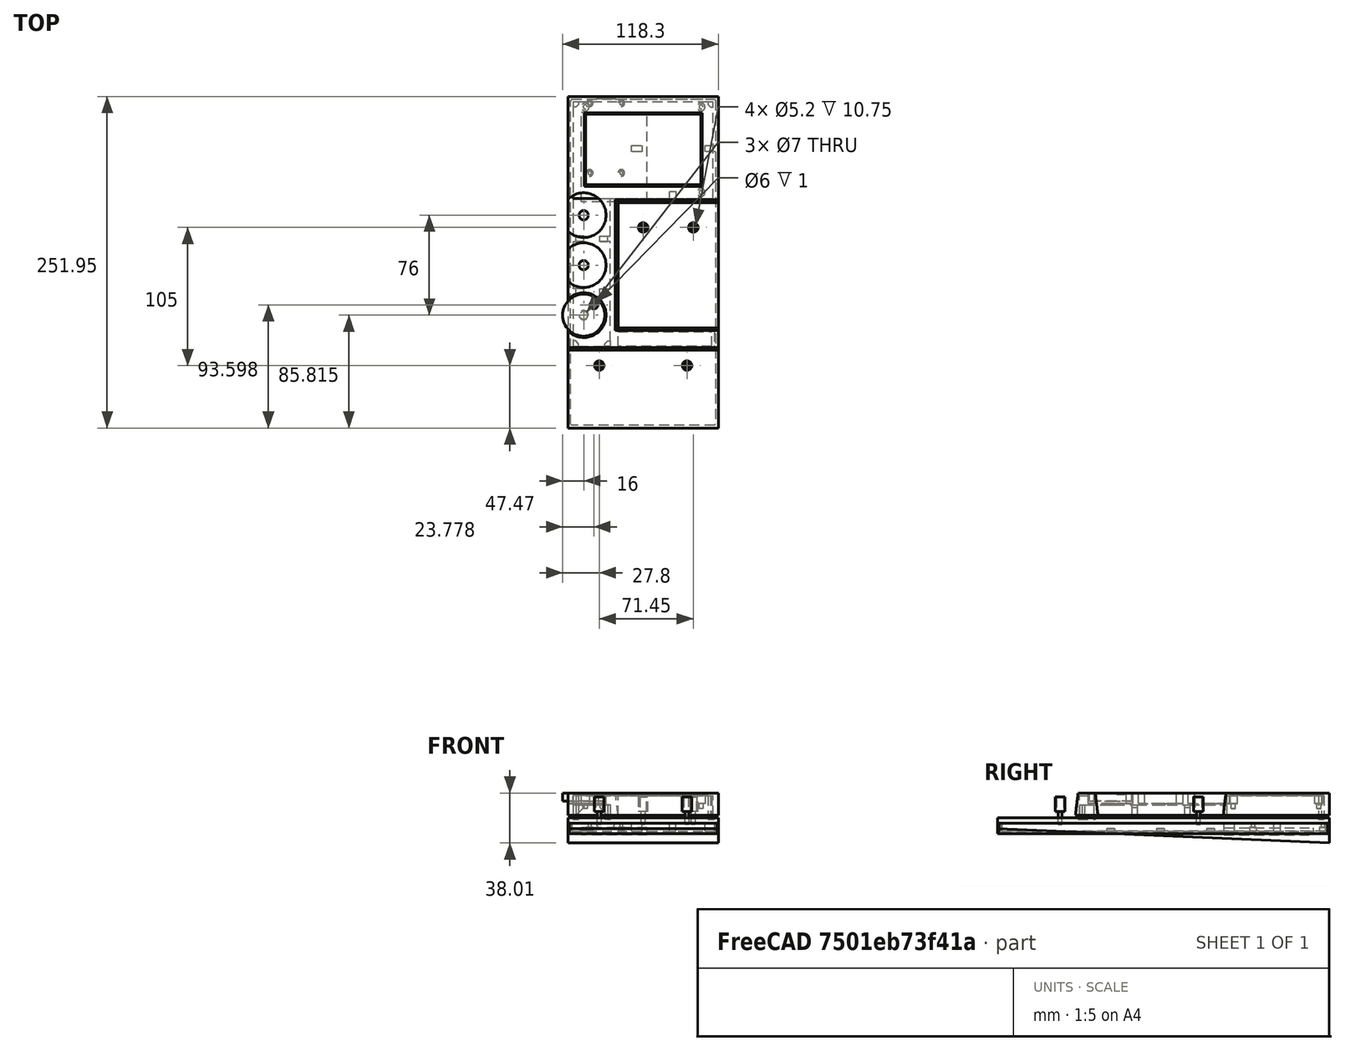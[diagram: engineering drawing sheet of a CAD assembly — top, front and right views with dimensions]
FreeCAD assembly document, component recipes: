
FREECAD ASSEMBLY — COMPONENT RECIPES ("20211026a")

This assembly document has 11 components, labeled P0..P10 below (a component is one placed body or linked part). 10 of them carry a construction recipe — the FreeCAD feature program that regenerates the part from scratch, quoted from this document or its linked companion documents; the rest are supplied as boundary geometry only. No exploded tour is included for this assembly.
COMPONENT P0 — recipe-attached ("TopShell", modeled in this document).
Construction recipe (the document's own serialized feature program — sketch geometry with constraints, then the solid features built on it; lengths are millimeters unless a unit is written):

FEATURE [Sketcher::SketchObject] Sketch005  label="NumpadLoftBottom"
  FullyConstrained = true
  MapMode = 5
  Support = -> [XY_Plane003]
  expr: Constraints[16] = 4 * 19.05
  expr: Constraints[17] = 5 * 19.05
  expr: Constraints[18] = <<var>>.vLCDPad * 2 + 53.7 + 2
  expr: Constraints[15] = <<var>>.vBoxWidth
  sketch-geometry (8):
    g0: LineSegment StartX=0 StartY=0 StartZ=0 EndX=114.3 EndY=0 EndZ=0
    g1: LineSegment StartX=114.3 StartY=0 StartZ=0 EndX=114.3 EndY=-80.5 EndZ=0
    g2: LineSegment StartX=114.3 StartY=-80.5 StartZ=0 EndX=38.1 EndY=-80.5 EndZ=0
    g3: LineSegment StartX=38.1 StartY=-80.5 StartZ=0 EndX=38.1 EndY=-175.75 EndZ=0
    g4: LineSegment StartX=38.1 StartY=-175.75 StartZ=0 EndX=114.3 EndY=-175.75 EndZ=0
    g5: LineSegment StartX=114.3 StartY=-175.75 StartZ=0 EndX=114.3 EndY=-192.8 EndZ=0
    g6: LineSegment StartX=114.3 StartY=-192.8 StartZ=0 EndX=0 EndY=-192.8 EndZ=0
    g7: LineSegment StartX=0 StartY=-192.8 StartZ=0 EndX=0 EndY=0 EndZ=0
  constraints (23):
    c: PointOnObject(g0,g-1)
    c: Coincident(g0,g1)
    c: Vertical(g1)
    c: Coincident(g1,g2)
    c: Horizontal(g2)
    c: Coincident(g2,g3)
    c: Vertical(g3)
    c: Coincident(g3,g4)
    c: Horizontal(g4)
    c: Coincident(g4,g5)
    c: Vertical(g5)
    c: Coincident(g5,g6)
    c: PointOnObject(g6,g-2)
    c: Horizontal(g6)
    c: Coincident(g6,g7)
    c: DistanceX(g6,g6) = 114.3
    c: DistanceX(g4,g4) = 76.2
    c: DistanceY(g3,g3) = 95.25
    c: DistanceY(g1,g1) = 80.5
    c: Equal(g6,g0)
    c: Coincident(g7,g0)
    c: Coincident(g-1,g0)
    c: DistanceY(g5,g5) = 17.05
FEATURE [Sketcher::SketchObject] Sketch006  label="NumpadLoftTop"
  AttachmentOffset = pos=(0,0,17) rot=(0,0,1;0rad)
  FullyConstrained = true
  MapMode = 5
  Placement = pos=(0,0,17) rot=(0,0,1;0rad)
  Support = -> [XY_Plane003]
  expr: Constraints[15] = <<var>>.vBoxWidth
  expr: Constraints[18] = <<var>>.vLCDPad * 2 + 53.7 + 2
  expr: Constraints[17] = 5 * 19.05
  expr: Constraints[16] = 4 * 19.05
  expr: .AttachmentOffset.Base.z = <<var>>.vTopHeight
  sketch-geometry (15):
    g0: LineSegment StartX=0 StartY=0 StartZ=0 EndX=114.3 EndY=0 EndZ=0
    g1: LineSegment StartX=114.3 StartY=0 StartZ=0 EndX=114.3 EndY=-80.5 EndZ=0
    g2: LineSegment StartX=114.3 StartY=-80.5 StartZ=0 EndX=38.1 EndY=-80.5 EndZ=0
    g3: LineSegment StartX=38.1 StartY=-80.5 StartZ=0 EndX=38.1 EndY=-175.75 EndZ=0
    g4: LineSegment StartX=38.1 StartY=-175.75 StartZ=0 EndX=114.3 EndY=-175.75 EndZ=0
    g5: LineSegment StartX=114.3 StartY=-175.75 StartZ=0 EndX=114.3 EndY=-192.8 EndZ=0
    g6: LineSegment StartX=114.3 StartY=-192.8 StartZ=0 EndX=0 EndY=-192.8 EndZ=0
    g7: LineSegment StartX=0 StartY=-192.8 StartZ=0 EndX=0 EndY=0 EndZ=0
    g8: LineSegment StartX=114.3 StartY=0 StartZ=0 EndX=114.3 EndY=-78.5 EndZ=0
    g9: LineSegment StartX=114.3 StartY=-78.5 StartZ=0 EndX=36.1 EndY=-78.5 EndZ=0
    g10: LineSegment StartX=36.1 StartY=-78.5 StartZ=0 EndX=36.1 EndY=-177.75 EndZ=0
    g11: LineSegment StartX=36.1 StartY=-177.75 StartZ=0 EndX=114.3 EndY=-177.75 EndZ=0
    g12: LineSegment StartX=114.3 StartY=-177.75 StartZ=0 EndX=114.3 EndY=-190.8 EndZ=0
    g13: LineSegment StartX=114.3 StartY=-190.8 StartZ=0 EndX=0 EndY=-190.8 EndZ=0
    g14: LineSegment StartX=0 StartY=-190.8 StartZ=0 EndX=0 EndY=0 EndZ=0
  constraints (43):
    c: PointOnObject(g0,g-1)
    c: Coincident(g0,g1)
    c: Vertical(g1)
    c: Coincident(g1,g2)
    c: Horizontal(g2)
    c: Coincident(g2,g3)
    c: Vertical(g3)
    c: Coincident(g3,g4)
    c: Horizontal(g4)
    c: Coincident(g4,g5)
    c: Vertical(g5)
    c: Coincident(g5,g6)
    c: PointOnObject(g6,g-2)
    c: Horizontal(g6)
    c: Coincident(g6,g7)
    c: DistanceX(g6,g6) = 114.3
    c: DistanceX(g4,g4) = 76.2
    c: DistanceY(g3,g3) = 95.25
    c: DistanceY(g1,g1) = 80.5
    c: Equal(g6,g0)
    c: Coincident(g7,g0)
    c: Coincident(g-1,g0)
    c: DistanceY(g5,g5) = 17.05
    c: Coincident(g0,g8)
    c: PointOnObject(g8,g1)
    c: Coincident(g8,g9)
    c: Horizontal(g9)
    c: Coincident(g9,g10)
    c: Vertical(g10)
    c: Coincident(g10,g11)
    c: PointOnObject(g11,g5)
    c: Horizontal(g11)
    c: DistanceY(g2,g9) = 2
    c: DistanceY(g10,g3) = 2
    c: DistanceX(g10,g3) = 2
    c: Coincident(g11,g12)
    c: PointOnObject(g12,g5)
    c: Coincident(g12,g13)
    c: PointOnObject(g13,g7)
    c: Horizontal(g13)
    c: Coincident(g13,g14)
    c: Coincident(g14,g0)
    c: DistanceY(g6,g13) = 2
FEATURE [PartDesign::AdditiveLoft] AdditiveLoft  label="NumpadLoft"
  Closed = false
  Profile = -> Sketch005
  Refine = true
  Ruled = false
  Sections = -> [Sketch006]
FEATURE [Sketcher::SketchObject] Sketch007
  FullyConstrained = true
  MapMode = 5
  Support = -> [XY_Plane003]
  expr: Constraints[8] = <<var>>.vLCDBezWidth
  expr: Constraints[9] = <<var>>.vLCDBezHeight
  expr: Constraints[10] = <<var>>.vLCDPad + 1
  expr: Constraints[11] = <<var>>.vLCDPad + 1
  sketch-geometry (4):
    g0: LineSegment StartX=13.4 StartY=-13.4 StartZ=0 EndX=100.9 EndY=-13.4 EndZ=0
    g1: LineSegment StartX=100.9 StartY=-13.4 StartZ=0 EndX=100.9 EndY=-67.1 EndZ=0
    g2: LineSegment StartX=100.9 StartY=-67.1 StartZ=0 EndX=13.4 EndY=-67.1 EndZ=0
    g3: LineSegment StartX=13.4 StartY=-67.1 StartZ=0 EndX=13.4 EndY=-13.4 EndZ=0
  constraints (12):
    c: Coincident(g0,g1)
    c: Coincident(g1,g2)
    c: Coincident(g2,g3)
    c: Coincident(g3,g0)
    c: Horizontal(g0)
    c: Horizontal(g2)
    c: Vertical(g1)
    c: Vertical(g3)
    c: DistanceX(g0,g0) = 87.5
    c: DistanceY(g3,g3) = 53.7
    c: DistanceX(g-1,g0) = 13.4
    c: DistanceY(g0,g-1) = 13.4
FEATURE [PartDesign::Pocket] Pocket001  label="PocketForScreen"
  BaseFeature = -> AdditiveLoft
  Length = 5
  Length2 = 100
  Profile = -> Sketch007
  Refine = true
  Reversed = true
  Type = 1
FEATURE [PartDesign::Chamfer] Chamfer
  Angle = 45
  Base = -> Pocket001 [Edge30,Edge36,Edge33,Edge35]
  BaseFeature = -> Pocket001
  ChamferType = 0
  FlipDirection = false
  Refine = true
  Size = 1
  Size2 = 1
  SupportTransform = false
FEATURE [PartDesign::Plane] DatumPlane001
  Length = 174.137
  Placement = pos=(0,0,17) rot=(0,0,1;0rad)
  ResizeMode = 0
  Width = 252.637
FEATURE [Sketcher::SketchObject] Sketch008
  ExternalGeometry = -> [Sketch006]
  FullyConstrained = true
  MapMode = 5
  Placement = pos=(0,0,17) rot=(0,0,1;0rad)
  Support = -> [DatumPlane001]
  sketch-geometry (6):
    g0: GeomPoint X=36.1 Y=-128.125 Z=0
    g1: Circle CenterX=12 CenterY=-128.125 CenterZ=0 NormalX=0 NormalY=0 NormalZ=1 AngleXU=0 Radius=17
    g2: Circle CenterX=12 CenterY=-90.125 CenterZ=0 NormalX=0 NormalY=0 NormalZ=1 AngleXU=0 Radius=17
    g3: Circle CenterX=12 CenterY=-166.125 CenterZ=0 NormalX=0 NormalY=0 NormalZ=1 AngleXU=0 Radius=17
    g4: LineSegment StartX=12 StartY=-90.125 StartZ=0 EndX=12 EndY=-128.125 EndZ=0
    g5: LineSegment StartX=12 StartY=-128.125 StartZ=0 EndX=12 EndY=-166.125 EndZ=0
  constraints (14):
    c: Symmetric(g-3,g-3,g0)
    c: Horizontal(g0,g1)
    c: DistanceX(g-1,g1) = 12  'ScrubberOffset'
    c: Equal(g1,g2)
    c: Equal(g1,g3)
    c: Vertical(g1,g3)
    c: Radius(g1) = 17  'ScrubberRadius'
    c: DistanceY(g3,g1) = 38  'ScrubberSpacing'
    c: Vertical(g1,g2)
    c: Coincident(g4,g2)
    c: Coincident(g4,g1)
    c: Coincident(g5,g1)
    c: Coincident(g5,g3)
    c: Equal(g4,g5)
FEATURE [PartDesign::Pocket] Pocket002  label="PocketForScrubbers"
  BaseFeature = -> Chamfer
  Length = 8
  Length2 = 100
  Profile = -> Sketch008
  Refine = true
  Type = 0
FEATURE [PartDesign::Plane] DatumPlane005
  Length = 174.137
  MapMode = 5
  Placement = pos=(0,0,0) rot=(1,0,0;3.14159rad)
  ResizeMode = 0
  Width = 252.637
FEATURE [Sketcher::SketchObject] Sketch022
  ExternalGeometry = -> [Pocket002]
  FullyConstrained = true
  MapMode = 5
  Placement = pos=(0,0,0) rot=(1,0,0;3.14159rad)
  Support = -> [DatumPlane005]
  sketch-geometry (10):
    g0: LineSegment StartX=0 StartY=0 StartZ=0 EndX=114.3 EndY=0 EndZ=0
    g1: LineSegment StartX=114.3 StartY=0 StartZ=0 EndX=114.3 EndY=80.5 EndZ=0
    g2: LineSegment StartX=114.3 StartY=80.5 StartZ=0 EndX=38.1 EndY=80.5 EndZ=0
    g3: LineSegment StartX=38.1 StartY=80.5 StartZ=0 EndX=38.1 EndY=67.1 EndZ=0
    g4: LineSegment StartX=38.1 StartY=67.1 StartZ=0 EndX=0 EndY=67.1 EndZ=0
    g5: LineSegment StartX=0 StartY=67.1 StartZ=0 EndX=0 EndY=0 EndZ=0
    g6: LineSegment StartX=4 StartY=77.5 StartZ=0 EndX=110.3 EndY=77.5 EndZ=0
    g7: LineSegment StartX=110.3 StartY=77.5 StartZ=0 EndX=110.3 EndY=4 EndZ=0
    g8: LineSegment StartX=110.3 StartY=4 StartZ=0 EndX=4 EndY=4 EndZ=0
    g9: LineSegment StartX=4 StartY=4 StartZ=0 EndX=4 EndY=77.5 EndZ=0
  constraints (27):
    c: Coincident(g-1,g0)
    c: PointOnObject(g0,g-1)
    c: Coincident(g0,g1)
    c: Coincident(g1,g-3)
    c: Coincident(g1,g2)
    c: Coincident(g2,g-4)
    c: Coincident(g2,g3)
    c: Vertical(g3)
    c: Coincident(g3,g4)
    c: Horizontal(g4)
    c: Coincident(g4,g5)
    c: Coincident(g5,g0)
    c: Vertical(g5)
    c: Vertical(g1)
    c: Horizontal(g-5,g3)
    c: Horizontal(g6)
    c: Coincident(g6,g7)
    c: Vertical(g7)
    c: Coincident(g7,g8)
    c: Horizontal(g8)
    c: Coincident(g8,g9)
    c: Vertical(g9)
    c: Distance(g6,g1) = 4
    c: Distance(g8,g0) = 4
    c: Distance(g8,g5) = 4
    c: Coincident(g9,g6)
    c: Distance(g6,g2) = 3
FEATURE [PartDesign::Pocket] Pocket006  label="PocketRearLCD"
  BaseFeature = -> Pocket002
  Length = 15
  Length2 = 100
  Profile = -> Sketch022
  Refine = true
  Type = 0
FEATURE [Sketcher::SketchObject] Sketch023
  ExternalGeometry = -> [Pocket006]
  FullyConstrained = true
  MapMode = 5
  Placement = pos=(0,0,0) rot=(1,0,0;3.14159rad)
  Support = -> [DatumPlane005]
  sketch-geometry (4):
    g0: LineSegment StartX=38.1 StartY=178.75 StartZ=0 EndX=111.3 EndY=178.75 EndZ=0
    g1: LineSegment StartX=111.3 StartY=178.75 StartZ=0 EndX=111.3 EndY=189.8 EndZ=0
    g2: LineSegment StartX=111.3 StartY=189.8 StartZ=0 EndX=38.1 EndY=189.8 EndZ=0
    g3: LineSegment StartX=38.1 StartY=189.8 StartZ=0 EndX=38.1 EndY=178.75 EndZ=0
  constraints (12):
    c: Coincident(g0,g1)
    c: Coincident(g1,g2)
    c: Coincident(g2,g3)
    c: Coincident(g3,g0)
    c: Horizontal(g0)
    c: Horizontal(g2)
    c: Vertical(g1)
    c: DistanceX(g1,g-4) = 3
    c: DistanceY(g-3,g0) = 3
    c: DistanceY(g1,g-4) = 3
    c: Vertical(g3)
    c: Vertical(g0,g-3)
FEATURE [PartDesign::Pocket] Pocket007  label="PocketRearChords"
  BaseFeature = -> Pocket006
  Length = 15
  Length2 = 100
  Profile = -> Sketch023
  Refine = true
  Type = 0
FEATURE [Sketcher::SketchObject] Sketch024
  ExternalGeometry = -> [Pocket007]
  FullyConstrained = true
  MapMode = 5
  Placement = pos=(0,0,0) rot=(1,0,0;3.14159rad)
  Support = -> [DatumPlane005]
  sketch-geometry (4):
    g0: LineSegment StartX=4 StartY=189.8 StartZ=0 EndX=32.1 EndY=189.8 EndZ=0
    g1: LineSegment StartX=32.1 StartY=189.8 StartZ=0 EndX=32.1 EndY=75.125 EndZ=0
    g2: LineSegment StartX=32.1 StartY=75.125 StartZ=0 EndX=4 EndY=75.125 EndZ=0
    g3: LineSegment StartX=4 StartY=75.125 StartZ=0 EndX=4 EndY=189.8 EndZ=0
  constraints (11):
    c: Coincident(g0,g1)
    c: Coincident(g1,g2)
    c: Coincident(g2,g3)
    c: Coincident(g3,g0)
    c: Horizontal(g0)
    c: Horizontal(g2)
    c: Vertical(g1)
    c: Vertical(g3)
    c: DistanceX(g1,g-4) = 6
    c: Horizontal(g-3,g0)
    c: Coincident(g2,g-5)
FEATURE [PartDesign::Pocket] Pocket008  label="PocketBehindScrubbers"
  BaseFeature = -> Pocket007
  Length = 8
  Length2 = 100
  Profile = -> Sketch024
  Refine = true
  Type = 0
FEATURE [Sketcher::SketchObject] Sketch025
  FullyConstrained = true
  MapMode = 5
  Support = -> [XY_Plane003]
  expr: Constraints[2] = 128.13 + 38
  sketch-geometry (5):
    g0: Circle CenterX=12 CenterY=-166.13 CenterZ=0 NormalX=0 NormalY=0 NormalZ=1 AngleXU=0 Radius=3.5
    g1: Circle CenterX=12 CenterY=-128.13 CenterZ=0 NormalX=0 NormalY=0 NormalZ=1 AngleXU=0 Radius=3.5
    g2: Circle CenterX=12 CenterY=-90.13 CenterZ=0 NormalX=0 NormalY=0 NormalZ=1 AngleXU=0 Radius=3.5
    g3: LineSegment StartX=12 StartY=-166.13 StartZ=0 EndX=12 EndY=-128.13 EndZ=0
    g4: LineSegment StartX=12 StartY=-128.13 StartZ=0 EndX=12 EndY=-90.13 EndZ=0
  constraints (13):
    c: Radius(g0) = 3.5  'ScrubberHole'
    c: DistanceX(g-1,g0) = 12
    c: DistanceY(g0,g-1) = 166.13
    c: Equal(g0,g1)
    c: Equal(g0,g2)
    c: Vertical(g0,g1)
    c: Vertical(g0,g2)
    c: Coincident(g3,g0)
    c: Coincident(g3,g1)
    c: Coincident(g4,g1)
    c: Coincident(g4,g2)
    c: Equal(g3,g4)
    c: DistanceY(g4,g4) = 38
FEATURE [PartDesign::Pocket] Pocket009  label="PocketEncoderHoles"
  BaseFeature = -> Pocket008
  Length = 5
  Length2 = 100
  Profile = -> Sketch025
  Refine = true
  Reversed = true
  Type = 1
FEATURE [Sketcher::SketchObject] Sketch026
  AttachmentOffset = pos=(0,0,15) rot=(0,0,1;0rad)
  FullyConstrained = true
  MapMode = 5
  Placement = pos=(0,0,15) rot=(0,0,1;0rad)
  Support = -> [XY_Plane003]
  expr: Constraints[7] = <<var>>.vLCDHolderX
  expr: Constraints[8] = <<var>>.vLCDHolderY
  sketch-geometry (3):
    g0: Circle CenterX=13.125 CenterY=-7.85 CenterZ=0 NormalX=0 NormalY=0 NormalZ=1 AngleXU=0 Radius=3
    g1: Circle CenterX=101.125 CenterY=-7.85 CenterZ=0 NormalX=0 NormalY=0 NormalZ=1 AngleXU=0 Radius=3
    g2: Circle CenterX=101.125 CenterY=-72.85 CenterZ=0 NormalX=0 NormalY=0 NormalZ=1 AngleXU=0 Radius=3
  constraints (9):
    c: Radius(g0) = 3  'Radius'
    c: Equal(g0,g1)
    c: Equal(g0,g2)
    c: DistanceX(g0,g1) = 88
    c: Horizontal(g0,g1)
    c: DistanceY(g2,g1) = 65
    c: Vertical(g2,g1)
    c: DistanceX(g0) = 13.125
    c: DistanceY(g0) = -7.85
FEATURE [PartDesign::Pad] Pad009  label="PadLCDHolderA"
  BaseFeature = -> Pocket009
  Direction = (1,1,1)
  Length = 6
  Length2 = 100
  Profile = -> Sketch026
  Refine = true
  Reversed = true
  Type = 0
FEATURE [Sketcher::SketchObject] Sketch027
  AttachmentOffset = pos=(0,0,15) rot=(0,0,1;0rad)
  FullyConstrained = true
  MapMode = 5
  Placement = pos=(0,0,15) rot=(0,0,1;0rad)
  Support = -> [XY_Plane003]
  expr: Constraints[8] = <<var>>.vLCDHolderY
  expr: Constraints[7] = <<var>>.vLCDHolderX
  sketch-geometry (3):
    g0: Circle CenterX=13.125 CenterY=-7.85 CenterZ=0 NormalX=0 NormalY=0 NormalZ=1 AngleXU=0 Radius=1.5
    g1: Circle CenterX=101.125 CenterY=-7.85 CenterZ=0 NormalX=0 NormalY=0 NormalZ=1 AngleXU=0 Radius=1.5
    g2: Circle CenterX=101.125 CenterY=-72.85 CenterZ=0 NormalX=0 NormalY=0 NormalZ=1 AngleXU=0 Radius=1.5
  constraints (9):
    c: Radius(g0) = 1.5  'Radius'
    c: Equal(g0,g1)
    c: Equal(g0,g2)
    c: DistanceX(g0,g1) = 88
    c: Horizontal(g0,g1)
    c: DistanceY(g2,g1) = 65
    c: Vertical(g2,g1)
    c: DistanceX(g0) = 13.125
    c: DistanceY(g0) = -7.85
FEATURE [PartDesign::Pad] Pad010  label="PadLCDHolderB"
  BaseFeature = -> Pad009
  Direction = (1,1,1)
  Length = 10
  Length2 = 100
  Profile = -> Sketch027
  Refine = true
  Reversed = true
  Type = 0
FEATURE [PartDesign::Plane] DatumPlane006
  Length = 174.137
  MapMode = 5
  Placement = pos=(0,0,8) rot=(1,0,0;3.14159rad)
  ResizeMode = 0
  Width = 252.637
FEATURE [Sketcher::SketchObject] Sketch028
  ExternalGeometry = -> [Pad010]
  FullyConstrained = true
  MapMode = 5
  Placement = pos=(0,0,8) rot=(1,0,0;3.14159rad)
  Support = -> [DatumPlane006]
  sketch-geometry (16):
    g0: LineSegment StartX=4 StartY=110 StartZ=0 EndX=12 EndY=110 EndZ=0
    g1: LineSegment StartX=12 StartY=110 StartZ=0 EndX=12 EndY=106 EndZ=0
    g2: LineSegment StartX=12 StartY=106 StartZ=0 EndX=4 EndY=106 EndZ=0
    g3: LineSegment StartX=4 StartY=106 StartZ=0 EndX=4 EndY=110 EndZ=0
    g4: LineSegment StartX=4 StartY=150 StartZ=0 EndX=12 EndY=150 EndZ=0
    g5: LineSegment StartX=12 StartY=150 StartZ=0 EndX=12 EndY=146 EndZ=0
    g6: LineSegment StartX=12 StartY=146 StartZ=0 EndX=4 EndY=146 EndZ=0
    g7: LineSegment StartX=4 StartY=146 StartZ=0 EndX=4 EndY=150 EndZ=0
    g8: LineSegment StartX=32.1 StartY=150 StartZ=0 EndX=24.1 EndY=150 EndZ=0
    g9: LineSegment StartX=24.1 StartY=150 StartZ=0 EndX=24.1 EndY=146 EndZ=0
    g10: LineSegment StartX=24.1 StartY=146 StartZ=0 EndX=32.1 EndY=146 EndZ=0
    g11: LineSegment StartX=32.1 StartY=146 StartZ=0 EndX=32.1 EndY=150 EndZ=0
    g12: LineSegment StartX=24.1 StartY=106 StartZ=0 EndX=32.1 EndY=106 EndZ=0
    g13: LineSegment StartX=32.1 StartY=106 StartZ=0 EndX=32.1 EndY=110 EndZ=0
    g14: LineSegment StartX=32.1 StartY=110 StartZ=0 EndX=24.1 EndY=110 EndZ=0
    g15: LineSegment StartX=24.1 StartY=110 StartZ=0 EndX=24.1 EndY=106 EndZ=0
  constraints (48):
    c: Coincident(g0,g1)
    c: Coincident(g1,g2)
    c: Coincident(g2,g3)
    c: Coincident(g3,g0)
    c: Horizontal(g0)
    c: Horizontal(g2)
    c: Vertical(g1)
    c: Vertical(g3)
    c: DistanceX(g2,g2) = 8
    c: DistanceX(g-1,g2) = 4
    c: DistanceY(g1,g1) = 4
    c: DistanceY(g-1,g2) = 106
    c: Coincident(g4,g5)
    c: Coincident(g5,g6)
    c: Coincident(g6,g7)
    c: Coincident(g7,g4)
    c: Horizontal(g4)
    c: Horizontal(g6)
    c: Vertical(g5)
    c: Vertical(g7)
    c: Coincident(g8,g9)
    c: Coincident(g9,g10)
    c: Coincident(g10,g11)
    c: Coincident(g11,g8)
    c: Horizontal(g8)
    c: Horizontal(g10)
    c: Vertical(g9)
    c: Vertical(g11)
    c: Coincident(g12,g13)
    c: Coincident(g13,g14)
    c: Coincident(g14,g15)
    c: Coincident(g15,g12)
    c: Horizontal(g12)
    c: Horizontal(g14)
    c: Vertical(g13)
    c: Vertical(g15)
    c: Vertical(g0,g6)
    c: Horizontal(g0,g14)
    c: Horizontal(g5,g9)
    c: Vertical(g-3,g12)
    c: Vertical(g10,g-3)
    c: Equal(g1,g15)
    c: Equal(g1,g9)
    c: Equal(g1,g5)
    c: Equal(g0,g14)
    c: Equal(g0,g10)
    c: Equal(g0,g6)
    c: DistanceY(g0,g6) = 36
FEATURE [PartDesign::Pad] Pad011  label="PadRibs"
  BaseFeature = -> Pad010
  Direction = (1,1,1)
  Length = 8
  Length2 = 100
  Profile = -> Sketch028
  Refine = true
  Type = 0
FEATURE [PartDesign::Chamfer] Chamfer008
  Angle = 45
  Base = -> Pad011 [Vertex107,Edge158,Edge153,Edge148,Edge162]
  BaseFeature = -> Pad011
  ChamferType = 0
  FlipDirection = false
  Refine = true
  Size = 6
  Size2 = 1
  SupportTransform = false
FEATURE [Sketcher::SketchObject] Sketch031
  AttachmentOffset = pos=(0,0,-7) rot=(0,0,1;0rad)
  ExternalGeometry = -> [Chamfer008]
  FullyConstrained = true
  MapMode = 5
  Placement = pos=(0,0,15) rot=(1,0,0;3.14159rad)
  Support = -> [DatumPlane006]
  sketch-geometry (16):
    g0: LineSegment StartX=4 StartY=189.8 StartZ=0 EndX=8 EndY=189.8 EndZ=0
    g1: LineSegment StartX=8 StartY=189.8 StartZ=0 EndX=8 EndY=185.8 EndZ=0
    g2: LineSegment StartX=8 StartY=185.8 StartZ=0 EndX=4 EndY=185.8 EndZ=0
    g3: LineSegment StartX=4 StartY=185.8 StartZ=0 EndX=4 EndY=189.8 EndZ=0
    g4: LineSegment StartX=32.1 StartY=189.8 StartZ=0 EndX=28.1 EndY=189.8 EndZ=0
    g5: LineSegment StartX=28.1 StartY=189.8 StartZ=0 EndX=28.1 EndY=185.8 EndZ=0
    g6: LineSegment StartX=28.1 StartY=185.8 StartZ=0 EndX=32.1 EndY=185.8 EndZ=0
    g7: LineSegment StartX=32.1 StartY=185.8 StartZ=0 EndX=32.1 EndY=189.8 EndZ=0
    g8: LineSegment StartX=4 StartY=4 StartZ=0 EndX=8 EndY=4 EndZ=0
    g9: LineSegment StartX=8 StartY=4 StartZ=0 EndX=8 EndY=8 EndZ=0
    g10: LineSegment StartX=8 StartY=8 StartZ=0 EndX=4 EndY=8 EndZ=0
    g11: LineSegment StartX=4 StartY=8 StartZ=0 EndX=4 EndY=4 EndZ=0
    g12: LineSegment StartX=110.3 StartY=4 StartZ=0 EndX=106.3 EndY=4 EndZ=0
    g13: LineSegment StartX=106.3 StartY=4 StartZ=0 EndX=106.3 EndY=8 EndZ=0
    g14: LineSegment StartX=106.3 StartY=8 StartZ=0 EndX=110.3 EndY=8 EndZ=0
    g15: LineSegment StartX=110.3 StartY=8 StartZ=0 EndX=110.3 EndY=4 EndZ=0
  constraints (44):
    c: Coincident(g0,g1)
    c: Coincident(g1,g2)
    c: Coincident(g2,g3)
    c: Coincident(g3,g0)
    c: Horizontal(g0)
    c: Horizontal(g2)
    c: Vertical(g1)
    c: Vertical(g3)
    c: Coincident(g0,g-3)
    c: DistanceY(g1,g1) = 4
    c: Equal(g1,g2)
    c: Coincident(g4,g5)
    c: Coincident(g5,g6)
    c: Coincident(g6,g7)
    c: Coincident(g7,g4)
    c: Horizontal(g4)
    c: Horizontal(g6)
    c: Vertical(g5)
    c: Vertical(g7)
    c: Coincident(g4,g-4)
    c: Equal(g2,g5)
    c: Equal(g2,g6)
    c: Coincident(g8,g9)
    c: Coincident(g9,g10)
    c: Coincident(g10,g11)
    c: Coincident(g11,g8)
    c: Horizontal(g8)
    c: Horizontal(g10)
    c: Vertical(g9)
    c: Vertical(g11)
    c: Coincident(g8,g-5)
    c: Coincident(g12,g13)
    c: Coincident(g13,g14)
    c: Coincident(g14,g15)
    c: Coincident(g15,g12)
    c: Horizontal(g12)
    c: Horizontal(g14)
    c: Vertical(g13)
    c: Vertical(g15)
    c: Coincident(g12,g-6)
    c: Equal(g2,g9)
    c: Equal(g9,g13)
    c: Equal(g9,g10)
    c: Equal(g9,g12)
FEATURE [PartDesign::Pad] Pad013
  BaseFeature = -> Chamfer008
  Direction = (1,1,1)
  Length = 18
  Length2 = 100
  Profile = -> Sketch031
  Refine = true
  Type = 0
FEATURE [PartDesign::Chamfer] Chamfer009
  Angle = 45
  Base = -> Pad013 [Edge104,Edge109,Edge209,Edge202]
  BaseFeature = -> Pad013
  ChamferType = 0
  FlipDirection = false
  Refine = true
  Size = 2
  Size2 = 1
  SupportTransform = false
FEATURE [PartDesign::Plane] DatumPlane008
  Length = 174.137
  MapMode = 5
  Placement = pos=(0,0,15) rot=(1,0,0;3.14159rad)
  ResizeMode = 0
  Width = 252.637
FEATURE [Sketcher::SketchObject] Sketch032
  ExternalGeometry = -> [Chamfer009]
  FullyConstrained = true
  MapMode = 5
  Placement = pos=(0,0,15) rot=(1,0,0;3.14159rad)
  Support = -> [DatumPlane008]
  sketch-geometry (4):
    g0: LineSegment StartX=111.3 StartY=190.8 StartZ=0 EndX=109.3 EndY=190.8 EndZ=0
    g1: LineSegment StartX=109.3 StartY=190.8 StartZ=0 EndX=109.3 EndY=177.8 EndZ=0
    g2: LineSegment StartX=109.3 StartY=177.8 StartZ=0 EndX=111.3 EndY=177.8 EndZ=0
    g3: LineSegment StartX=111.3 StartY=177.8 StartZ=0 EndX=111.3 EndY=190.8 EndZ=0
  constraints (12):
    c: Coincident(g0,g1)
    c: Coincident(g1,g2)
    c: Coincident(g2,g3)
    c: Coincident(g3,g0)
    c: Horizontal(g0)
    c: Horizontal(g2)
    c: Vertical(g1)
    c: Vertical(g3)
    c: DistanceY(g3,g3) = 13
    c: DistanceX(g0,g0) = 2
    c: Vertical(g-3,g0)
    c: DistanceY(g-3,g0) = 1
FEATURE [PartDesign::Pad] Pad014
  BaseFeature = -> Chamfer009
  Direction = (1,1,1)
  Length = 18
  Length2 = 100
  Profile = -> Sketch032
  Refine = true
  Type = 0
FEATURE [PartDesign::Body] Body003  label="TopShell"
  Group = -> [Sketch005,Sketch006,AdditiveLoft,Sketch007,Pocket001,Chamfer,DatumPlane001,Sketch008,Pocket002,DatumPlane005,Sketch022,Pocket006,Sketch023,Pocket007,Sketch024,Pocket008,Sketch025,Pocket009,Sketch026,Pad009,Sketch027,Pad010,DatumPlane006,Sketch028,Pad011,Chamfer008,Sketch031,Pad013,Chamfer009,DatumPlane008,Sketch032,Pad014]
  Origin = -> Origin003
  Placement = pos=(-57.15,125.975,17) rot=(0,0,1;0rad)
  Tip = -> Pad014
  expr: .Placement.Base.x = <<var>>.vBoxWidth / -2
  expr: .Placement.Base.y = <<var>>.vBoxDepth / 2
COMPONENT P1 — recipe-attached ("Body004", modeled in this document).
Construction recipe (the document's own serialized feature program — sketch geometry with constraints, then the solid features built on it; lengths are millimeters unless a unit is written):

FEATURE [PartDesign::AdditiveCylinder] Cylinder
  Angle = 360
  AttacherType = Attacher::AttachEngine3D
  Height = 6
  Radius = 16
  Refine = true
FEATURE [Sketcher::SketchObject] Sketch009
  AttachmentOffset = pos=(0,0,6) rot=(0,0,1;0rad)
  FullyConstrained = true
  MapMode = 5
  Placement = pos=(0,0,6) rot=(0,0,1;0rad)
  Support = -> [XY_Plane004]
  sketch-geometry (2):
    g0: Circle CenterX=7.77817 CenterY=7.77817 CenterZ=0 NormalX=0 NormalY=0 NormalZ=1 AngleXU=0 Radius=3
    g1: LineSegment StartX=7.77817 StartY=7.77817 StartZ=0 EndX=-9e-16 EndY=0 EndZ=0
  constraints (5):
    c: Radius(g0) = 3
    c: Coincident(g1,g0)
    c: Coincident(g1,g-1)
    c: Distance(g1) = 11
    c: Angle(g-1,g1) = 0.785398
FEATURE [PartDesign::Pocket] Pocket003
  BaseFeature = -> Cylinder
  Length = 1
  Length2 = 100
  Profile = -> Sketch009
  Refine = true
  Type = 0
FEATURE [PartDesign::Body] Body004
  Group = -> [Cylinder,Sketch009,Pocket003]
  Origin = -> Origin004
  Placement = pos=(-45.15,-40.15,28) rot=(0,0,1;0rad)
  Tip = -> Pocket003
  expr: .Placement.Base.y = <<var>>.vScrubY
  expr: .Placement.Base.x = <<var>>.vScrubX
COMPONENT P2 — recipe-attached ("LiPo_605028", modeled in this document).
Construction recipe (the document's own serialized feature program — sketch geometry with constraints, then the solid features built on it; lengths are millimeters unless a unit is written):

FEATURE [PartDesign::AdditiveBox] Box
  AttacherType = Attacher::AttachEngine3D
  Height = 5.6
  Length = 68
  Refine = true
  Width = 50
FEATURE [PartDesign::Body] Body005  label="LiPo_605028"
  Group = -> [Box]
  Origin = -> Origin005
  Placement = pos=(3,46,2) rot=(0,0,1;1.5708rad)
  Tip = -> Box
COMPONENT P3 — recipe-attached ("M3_Cutout", modeled in this document).
Construction recipe (the document's own serialized feature program — sketch geometry with constraints, then the solid features built on it; lengths are millimeters unless a unit is written):

FEATURE [Sketcher::SketchObject] Sketch016
  FullyConstrained = true
  MapMode = 5
  Support = -> [XY_Plane008]
  sketch-geometry (1):
    g0: Circle CenterX=0 CenterY=0 CenterZ=0 NormalX=0 NormalY=0 NormalZ=1 AngleXU=0 Radius=1.5
  constraints (2):
    c: Coincident(g0,g-1)
    c: Radius(g0) = 1.5
FEATURE [PartDesign::Pad] Pad004
  Direction = (1,1,1)
  Length = 10
  Length2 = 100
  Profile = -> Sketch016
  Refine = true
  Reversed = true
  Type = 0
FEATURE [PartDesign::Body] Body008  label="M3_Cutout"
  Group = -> [Sketch016,Pad004]
  Origin = -> Origin008
  Placement = pos=(0,0,21) rot=(0,0,1;0rad)
  Tip = -> Pad004
COMPONENT P4 — recipe-attached ("BottomShell5degree", modeled in this document).
Construction recipe (the document's own serialized feature program — sketch geometry with constraints, then the solid features built on it; lengths are millimeters unless a unit is written):

FEATURE [Sketcher::SketchObject] Sketch029
  FullyConstrained = true
  MapMode = 5
  Support = -> [XY_Plane009]
  expr: Constraints[8] = <<var>>.vBoxWidth
  expr: Constraints[9] = <<var>>.vBoxDepth
  sketch-geometry (4):
    g0: LineSegment StartX=-57.15 StartY=125.975 StartZ=0 EndX=57.15 EndY=125.975 EndZ=0
    g1: LineSegment StartX=57.15 StartY=125.975 StartZ=0 EndX=57.15 EndY=-125.975 EndZ=0
    g2: LineSegment StartX=57.15 StartY=-125.975 StartZ=0 EndX=-57.15 EndY=-125.975 EndZ=0
    g3: LineSegment StartX=-57.15 StartY=-125.975 StartZ=0 EndX=-57.15 EndY=125.975 EndZ=0
  constraints (11):
    c: Coincident(g0,g1)
    c: Coincident(g1,g2)
    c: Coincident(g2,g3)
    c: Coincident(g3,g0)
    c: Horizontal(g0)
    c: Horizontal(g2)
    c: Vertical(g1)
    c: Vertical(g3)
    c: DistanceX(g0,g0) = 114.3
    c: DistanceY(g3,g3) = 251.95
    c: Symmetric(g0,g1,g-1)
FEATURE [PartDesign::Plane] DatumPlane007
  Length = 67.4311
  Placement = pos=(0,-125.975,0) rot=(-1,0,0;0.043633rad)
  ResizeMode = 0
  Width = 169.353
  expr: .Placement.Base.y = <<var>>.vBoxDepth / -2
FEATURE [PartDesign::Pad] Pad012
  Direction = (1,1,1)
  Length = 100
  Length2 = 100
  Profile = -> Sketch029
  Refine = true
  Reversed = true
  Type = 0
FEATURE [Sketcher::SketchObject] Sketch030
  AttachmentOffset = pos=(0,0,-8) rot=(0,0,1;0rad)
  FullyConstrained = false
  MapMode = 5
  Placement = pos=(0,-126.324,-7.99239) rot=(-1,0,0;0.043633rad)
  Support = -> [DatumPlane007]
  expr: .AttachmentOffset.Base.z = 0 - <<var>>.vBotHeight
  sketch-geometry (4):
    g0: LineSegment StartX=-82.8874 StartY=275.049 StartZ=0 EndX=82.0576 EndY=275.049 EndZ=0
    g1: LineSegment StartX=82.0576 StartY=275.049 StartZ=0 EndX=82.0576 EndY=-29.3715 EndZ=0
    g2: LineSegment StartX=82.0576 StartY=-29.3715 StartZ=0 EndX=-82.8874 EndY=-29.3715 EndZ=0
    g3: LineSegment StartX=-82.8874 StartY=-29.3715 StartZ=0 EndX=-82.8874 EndY=275.049 EndZ=0
  constraints (8):
    c: Coincident(g0,g1)
    c: Coincident(g1,g2)
    c: Coincident(g2,g3)
    c: Coincident(g3,g0)
    c: Horizontal(g0)
    c: Horizontal(g2)
    c: Vertical(g1)
    c: Vertical(g3)
FEATURE [PartDesign::Pocket] Pocket010
  BaseFeature = -> Pad012
  Length = 5
  Length2 = 100
  Profile = -> Sketch030
  Refine = true
  Type = 1
FEATURE [PartDesign::Body] Body009  label="BottomShell5degree"
  Group = -> [Sketch029,DatumPlane007,Pad012,Sketch030,Pocket010]
  Origin = -> Origin009
  Placement = pos=(0,0,15) rot=(0,0,1;0rad)
  Tip = -> Pocket010
COMPONENT P5 — recipe-attached ("LCD_128x64", modeled in this document).
Construction recipe (the document's own serialized feature program — sketch geometry with constraints, then the solid features built on it; lengths are millimeters unless a unit is written):

FEATURE [Sketcher::SketchObject] Sketch014
  FullyConstrained = true
  MapMode = 5
  Support = -> [XY_Plane007]
  sketch-geometry (2):
    g0: Circle CenterX=0 CenterY=0 CenterZ=0 NormalX=0 NormalY=0 NormalZ=1 AngleXU=0 Radius=2.6
    g1: Circle CenterX=0 CenterY=0 CenterZ=0 NormalX=0 NormalY=0 NormalZ=1 AngleXU=0 Radius=3.6
  constraints (4):
    c: Radius(g0) = 2.6
    c: Coincident(g1,g0)
    c: Radius(g1) = 3.6
    c: Coincident(g0,g-1)
FEATURE [PartDesign::Pad] Pad003
  Direction = (1,1,1)
  Length = 11
  Length2 = 100
  Profile = -> Sketch014
  Refine = true
  Type = 0
FEATURE [PartDesign::Chamfer] Chamfer002
  Angle = 45
  Base = -> Pad003 [Edge6]
  BaseFeature = -> Pad003
  ChamferType = 0
  FlipDirection = false
  Refine = true
  Size = 0.25
  Size2 = 1
  SupportTransform = false
FEATURE [PartDesign::Body] Body007  label="HeatSetInsert"
  Group = -> [Sketch014,Pad003,Chamfer002]
  Origin = -> Origin007
  Placement = pos=(0,0,5) rot=(0,0,1;0rad)
  Tip = -> Chamfer002
COMPONENT P6 — geometry summary ("MiddlePlateClone"; no construction recipe available for this part):
  bounding box: 251.9 x 114.3 x 2.0 mm
  tessellated surface: 1,752 triangles
  volume: 21831 mm^3 (38% of its bounding box)
  symmetry: mirror-symmetric across its z mid-plane
COMPONENT P7 — recipe-attached ("FireBeetleMCU", modeled in this document).
Construction recipe (the document's own serialized feature program — sketch geometry with constraints, then the solid features built on it; lengths are millimeters unless a unit is written):

FEATURE [Sketcher::SketchObject] Sketch
  FullyConstrained = true
  MapMode = 5
  Support = -> [XY_Plane]
  expr: Constraints[8] = <<var>>.vBoxWidth
  expr: Constraints[9] = <<var>>.vBoxDepth
  sketch-geometry (4):
    g0: LineSegment StartX=-57.15 StartY=125.975 StartZ=0 EndX=57.15 EndY=125.975 EndZ=0
    g1: LineSegment StartX=57.15 StartY=125.975 StartZ=0 EndX=57.15 EndY=-125.975 EndZ=0
    g2: LineSegment StartX=57.15 StartY=-125.975 StartZ=0 EndX=-57.15 EndY=-125.975 EndZ=0
    g3: LineSegment StartX=-57.15 StartY=-125.975 StartZ=0 EndX=-57.15 EndY=125.975 EndZ=0
  constraints (11):
    c: Coincident(g0,g1)
    c: Coincident(g1,g2)
    c: Coincident(g2,g3)
    c: Coincident(g3,g0)
    c: Horizontal(g0)
    c: Horizontal(g2)
    c: Vertical(g1)
    c: Vertical(g3)
    c: DistanceX(g0,g0) = 114.3
    c: DistanceY(g3,g3) = 251.95
    c: Symmetric(g0,g1,g-1)
FEATURE [PartDesign::Pad] Pad
  Direction = (1,1,1)
  Length = 8
  Length2 = 100
  Profile = -> Sketch
  Refine = true
  Type = 0
  expr: Length = <<var>>.vBotHeight
FEATURE [PartDesign::Plane] DatumPlane
  Length = 148.24
  MapMode = 5
  Placement = pos=(0,0,8) rot=(0,0,1;0rad)
  ResizeMode = 0
  Support = -> [Pad]
  Width = 285.89
FEATURE [Sketcher::SketchObject] Sketch001
  FullyConstrained = true
  MapMode = 5
  Placement = pos=(0,0,8) rot=(0,0,1;0rad)
  Support = -> [DatumPlane]
  expr: Constraints[8] = <<var>>.vBoxWidth - <<var>>.vWallThk * 2
  expr: Constraints[9] = <<var>>.vBoxDepth - <<var>>.vWallThk * 2
  sketch-geometry (4):
    g0: LineSegment StartX=-55.15 StartY=123.975 StartZ=0 EndX=55.15 EndY=123.975 EndZ=0
    g1: LineSegment StartX=55.15 StartY=123.975 StartZ=0 EndX=55.15 EndY=-123.975 EndZ=0
    g2: LineSegment StartX=55.15 StartY=-123.975 StartZ=0 EndX=-55.15 EndY=-123.975 EndZ=0
    g3: LineSegment StartX=-55.15 StartY=-123.975 StartZ=0 EndX=-55.15 EndY=123.975 EndZ=0
  constraints (11):
    c: Coincident(g0,g1)
    c: Coincident(g1,g2)
    c: Coincident(g2,g3)
    c: Coincident(g3,g0)
    c: Horizontal(g0)
    c: Horizontal(g2)
    c: Vertical(g1)
    c: Vertical(g3)
    c: DistanceX(g0,g0) = 110.3
    c: DistanceY(g3,g3) = 247.95
    c: Symmetric(g0,g1,g-1)
FEATURE [PartDesign::Pocket] Pocket
  BaseFeature = -> Pad
  Length = 6
  Length2 = 100
  Profile = -> Sketch001
  Refine = true
  Type = 0
  expr: Length = <<var>>.vBotHeight - <<var>>.vWallThk
FEATURE [PartDesign::Chamfer] Chamfer004
  Angle = 45
  Base = -> Pocket [Edge2,Edge1,Edge5,Edge8,Edge20,Edge22,Edge17,Edge18]
  BaseFeature = -> Pocket
  ChamferType = 0
  FlipDirection = false
  Refine = true
  Size = 1
  Size2 = 1
  SupportTransform = false
FEATURE [PartDesign::Plane] DatumPlane003
  Length = 148.24
  MapMode = 5
  Placement = pos=(0,0,2) rot=(0,0,1;0rad)
  ResizeMode = 0
  Width = 285.89
FEATURE [Sketcher::SketchObject] Sketch017
  FullyConstrained = true
  MapMode = 5
  Placement = pos=(0,0,2) rot=(0,0,1;0rad)
  Support = -> [DatumPlane003]
  sketch-geometry (7):
    g0: Circle CenterX=-40.575 CenterY=121 CenterZ=0 NormalX=0 NormalY=0 NormalZ=1 AngleXU=0 Radius=2.5
    g1: Circle CenterX=-40.575 CenterY=68 CenterZ=0 NormalX=0 NormalY=0 NormalZ=1 AngleXU=0 Radius=2.5
    g2: Circle CenterX=-16.575 CenterY=68 CenterZ=0 NormalX=0 NormalY=0 NormalZ=1 AngleXU=0 Radius=2.5
    g3: Circle CenterX=-16.575 CenterY=121 CenterZ=0 NormalX=0 NormalY=0 NormalZ=1 AngleXU=0 Radius=2.5
    g4: GeomPoint X=-28.575 Y=68 Z=0
    g5: GeomPoint X=-57.15 Y=0 Z=0
    g6: GeomPoint X=-28.575 Y=0 Z=0
  constraints (16):
    c: Radius(g0) = 2.5  'Radius'
    c: Equal(g0,g3)
    c: Equal(g2,g0)
    c: Equal(g0,g1)
    c: DistanceX(g1,g2) = 24  'HorizontalCL'
    c: DistanceY(g1,g0) = 53  'VerticalCL'
    c: Horizontal(g1,g2)
    c: Horizontal(g0,g3)
    c: Vertical(g0,g1)
    c: Vertical(g3,g2)
    c: Symmetric(g1,g2,g4)
    c: Horizontal(g5,g-1)
    c: DistanceX(g5,g-1) = 57.15
    c: Symmetric(g5,g-1,g6)
    c: Vertical(g4,g6)
    c: DistanceY(g-1,g2) = 68  'VerticalOD'
FEATURE [PartDesign::Pad] Pad005
  BaseFeature = -> Chamfer004
  Direction = (1,1,1)
  Length = 3
  Length2 = 100
  Profile = -> Sketch017
  Refine = true
  Type = 0
FEATURE [Sketcher::SketchObject] Sketch018
  ExternalGeometry = -> [Pad005]
  FullyConstrained = true
  MapMode = 5
  Placement = pos=(0,0,2) rot=(0,0,1;0rad)
  Support = -> [DatumPlane003]
  sketch-geometry (4):
    g0: Circle CenterX=-40.575 CenterY=121 CenterZ=0 NormalX=0 NormalY=0 NormalZ=1 AngleXU=0 Radius=1.25
    g1: Circle CenterX=-16.575 CenterY=121 CenterZ=0 NormalX=0 NormalY=0 NormalZ=1 AngleXU=0 Radius=1.25
    g2: Circle CenterX=-40.575 CenterY=68 CenterZ=0 NormalX=0 NormalY=0 NormalZ=1 AngleXU=0 Radius=1.25
    g3: Circle CenterX=-16.575 CenterY=68 CenterZ=0 NormalX=0 NormalY=0 NormalZ=1 AngleXU=0 Radius=1.25
  constraints (8):
    c: Radius(g0) = 1.25  'Radius'
    c: Equal(g0,g1)
    c: Equal(g0,g3)
    c: Equal(g0,g2)
    c: Coincident(g-3,g0)
    c: Coincident(g-4,g1)
    c: Coincident(g-5,g2)
    c: Coincident(g3,g-6)
FEATURE [PartDesign::Pad] Pad006
  BaseFeature = -> Pad005
  Direction = (1,1,1)
  Length = 6
  Length2 = 100
  Profile = -> Sketch018
  Refine = true
  Type = 0
FEATURE [PartDesign::Plane] DatumPlane004
  Length = 60
  MapMode = 5
  Placement = pos=(0,125.975,0) rot=(0,0.707107,0.707107;3.14159rad)
  ResizeMode = 0
  Width = 60
FEATURE [Sketcher::SketchObject] Sketch019
  FullyConstrained = true
  MapMode = 5
  Placement = pos=(0,125.975,0) rot=(0,0.707107,0.707107;3.14159rad)
  Support = -> [DatumPlane004]
  sketch-geometry (12):
    g0: GeomPoint X=57.15 Y=0 Z=0
    g1: LineSegment StartX=0 StartY=0 StartZ=0 EndX=28.575 EndY=0 EndZ=0
    g2: LineSegment StartX=28.575 StartY=0 StartZ=0 EndX=57.15 EndY=0 EndZ=0
    g3: LineSegment StartX=21.575 StartY=16 StartZ=0 EndX=35.575 EndY=16 EndZ=0
    g4: LineSegment StartX=35.575 StartY=16 StartZ=0 EndX=35.575 EndY=8 EndZ=0
    g5: LineSegment StartX=31.575 StartY=4 StartZ=0 EndX=25.575 EndY=4 EndZ=0
    g6: LineSegment StartX=21.575 StartY=8 StartZ=0 EndX=21.575 EndY=16 EndZ=0
    g7: ArcOfCircle CenterX=25.575 CenterY=8 CenterZ=0 NormalX=0 NormalY=0 NormalZ=1 AngleXU=0 Radius=4 StartAngle=3.14159 EndAngle=4.71239
    g8: ArcOfCircle CenterX=31.575 CenterY=8 CenterZ=0 NormalX=0 NormalY=0 NormalZ=1 AngleXU=0 Radius=4 StartAngle=4.71239 EndAngle=6.28319
    g9: GeomPoint X=28.575 Y=8 Z=0
    g10: LineSegment StartX=25.575 StartY=8 StartZ=0 EndX=28.575 EndY=8 EndZ=0
    g11: LineSegment StartX=31.575 StartY=8 StartZ=0 EndX=28.575 EndY=8 EndZ=0
  constraints (29):
    c: PointOnObject(g0,g-1)
    c: DistanceX(g-1,g0) = 57.15
    c: Coincident(g-1,g1)
    c: Coincident(g2,g0)
    c: Equal(g1,g2)
    c: Horizontal(g1,g1)
    c: Coincident(g1,g2)
    c: Coincident(g3,g4)
    c: Coincident(g6,g3)
    c: Horizontal(g3)
    c: Horizontal(g5)
    c: Vertical(g4)
    c: Vertical(g6)
    c: Tangent(g6,g7) = 1.5708
    c: Tangent(g5,g7) = 1.5708
    c: Tangent(g5,g8) = 1.5708
    c: Tangent(g4,g8) = 1.5708
    c: Coincident(g10,g7)
    c: Coincident(g10,g9)
    c: Coincident(g11,g8)
    c: Coincident(g11,g10)
    c: Horizontal(g9,g7)
    c: Horizontal(g9,g8)
    c: Vertical(g1,g9)
    c: Equal(g10,g11)
    c: DistanceX(g3,g3) = 14  'Width'
    c: Radius(g7) = 4  'Radius'
    c: DistanceY(g-1,g5) = 4  'VertOffset'
    c: DistanceY(g6,g6) = 8
FEATURE [PartDesign::Pocket] Pocket005
  BaseFeature = -> Pad006
  Length = 5
  Length2 = 100
  Profile = -> Sketch019
  Refine = true
  Type = 0
FEATURE [Sketcher::SketchObject] Sketch020
  FullyConstrained = true
  MapMode = 5
  Placement = pos=(0,0,2) rot=(0,0,1;0rad)
  Support = -> [DatumPlane003]
  sketch-geometry (3):
    g0: Circle CenterX=-45 CenterY=35.75 CenterZ=0 NormalX=0 NormalY=0 NormalZ=1 AngleXU=0 Radius=3
    g1: Circle CenterX=-45 CenterY=-2.25 CenterZ=0 NormalX=0 NormalY=0 NormalZ=1 AngleXU=0 Radius=3
    g2: Circle CenterX=-45 CenterY=-40.25 CenterZ=0 NormalX=0 NormalY=0 NormalZ=1 AngleXU=0 Radius=3
  constraints (9):
    c: Radius(g0) = 3
    c: Equal(g0,g1)
    c: Equal(g0,g2)
    c: Vertical(g0,g1)
    c: Vertical(g0,g2)
    c: DistanceY(g1,g0) = 38
    c: DistanceY(g2,g1) = 38
    c: DistanceX(g0) = -45
    c: DistanceY(g0) = 35.75
FEATURE [PartDesign::Pad] Pad007
  BaseFeature = -> Pocket005
  Direction = (1,1,1)
  Length = 2
  Length2 = 100
  Profile = -> Sketch020
  Refine = true
  Type = 0
FEATURE [Sketcher::SketchObject] Sketch021
  FullyConstrained = true
  MapMode = 5
  Placement = pos=(0,0,2) rot=(0,0,1;0rad)
  Support = -> [DatumPlane003]
  sketch-geometry (12):
    g0: LineSegment StartX=47.15 StartY=89 StartZ=0 EndX=55.15 EndY=89 EndZ=0
    g1: LineSegment StartX=55.15 StartY=89 StartZ=0 EndX=55.15 EndY=84 EndZ=0
    g2: LineSegment StartX=55.15 StartY=84 StartZ=0 EndX=47.15 EndY=84 EndZ=0
    g3: LineSegment StartX=47.15 StartY=84 StartZ=0 EndX=47.15 EndY=89 EndZ=0
    g4: LineSegment StartX=-8.85 StartY=89 StartZ=0 EndX=-0.85 EndY=89 EndZ=0
    g5: LineSegment StartX=-0.85 StartY=89 StartZ=0 EndX=-0.85 EndY=84 EndZ=0
    g6: LineSegment StartX=-0.85 StartY=84 StartZ=0 EndX=-8.85 EndY=84 EndZ=0
    g7: LineSegment StartX=-8.85 StartY=84 StartZ=0 EndX=-8.85 EndY=89 EndZ=0
    g8: LineSegment StartX=20 StartY=54 StartZ=0 EndX=25 EndY=54 EndZ=0
    g9: LineSegment StartX=25 StartY=54 StartZ=0 EndX=25 EndY=46 EndZ=0
    g10: LineSegment StartX=25 StartY=46 StartZ=0 EndX=20 EndY=46 EndZ=0
    g11: LineSegment StartX=20 StartY=46 StartZ=0 EndX=20 EndY=54 EndZ=0
  constraints (36):
    c: Coincident(g0,g1)
    c: Coincident(g1,g2)
    c: Coincident(g2,g3)
    c: Coincident(g3,g0)
    c: Horizontal(g0)
    c: Horizontal(g2)
    c: Vertical(g1)
    c: Vertical(g3)
    c: Coincident(g4,g5)
    c: Coincident(g5,g6)
    c: Coincident(g6,g7)
    c: Coincident(g7,g4)
    c: Horizontal(g4)
    c: Horizontal(g6)
    c: Vertical(g5)
    c: Vertical(g7)
    c: Coincident(g8,g9)
    c: Coincident(g9,g10)
    c: Coincident(g10,g11)
    c: Coincident(g11,g8)
    c: Horizontal(g8)
    c: Horizontal(g10)
    c: Vertical(g9)
    c: Vertical(g11)
    c: DistanceY(g7,g7) = 5
    c: Equal(g7,g1)
    c: Equal(g7,g10)
    c: DistanceX(g6,g6) = 8
    c: Equal(g4,g0)
    c: Equal(g4,g11)
    c: DistanceX(g-1,g1) = 55.15
    c: DistanceX(g5,g2) = 48
    c: Horizontal(g5,g2)
    c: DistanceY(g-1,g5) = 84
    c: DistanceX(g10) = 20
    c: DistanceY(g10) = 46
FEATURE [PartDesign::Pad] Pad008
  BaseFeature = -> Pad007
  Direction = (1,1,1)
  Length = 6
  Length2 = 100
  Profile = -> Sketch021
  Refine = true
  Type = 0
FEATURE [PartDesign::Body] Body  label="BottomShell"
  Group = -> [Sketch,Pad,DatumPlane,Sketch001,Pocket,Chamfer004,DatumPlane003,Sketch017,Pad005,Sketch018,Pad006,DatumPlane004,Sketch019,Pocket005,Sketch020,Pad007,Sketch021,Pad008]
  Origin = -> Origin
  Placement = pos=(0,0,3) rot=(0,0,1;0rad)
  Tip = -> Pad008
COMPONENT P8 — recipe-attached ("EC11_Encoder", a linked part whose construction recipe lives in a companion FreeCAD document of the same project; that document's serialized recipe follows).
Construction recipe (the companion document, serialized — sketch geometry with constraints, then the solid features built on it; lengths are millimeters unless a unit is written):

FCSTD DOCUMENT  (FreeCAD 0.19R24276 (Git))
Label: EC11
License: All rights reserved
LicenseURL: http://en.wikipedia.org/wiki/All_rights_reserved
objects: PartDesign::AdditiveBox×1, PartDesign::AdditiveCylinder×1, PartDesign::Body×1
note: 5 computed .brp shape members not serialized (recipe doc carries the construction recipe); baked Part::Feature solids carry a one-line shape summary decoded from their .brp

FEATURE [PartDesign::AdditiveBox] Box012
  AttacherType = Attacher::AttachEngine3D
  AttachmentOffset = pos=(-6,-6,0) rot=(0,0,1;0rad)
  Height = 8.6
  Length = 12
  MapMode = 5
  Placement = pos=(-6,-6,0) rot=(0,0,1;0rad)
  Refine = true
  Support = -> [XY_Plane029]
  Width = 12
FEATURE [PartDesign::AdditiveCylinder] Cylinder003
  Angle = 360
  AttacherType = Attacher::AttachEngine3D
  BaseFeature = -> Box012
  Height = 25
  Radius = 3
  Refine = true
FEATURE [PartDesign::Body] Body026003  label="EC11_Encoder"
  Group = -> [Box012,Cylinder003]
  Origin = -> Origin029
  Tip = -> Cylinder003
COMPONENT P9 — same part as P7; its construction recipe is shown at P7.
COMPONENT P10 — same part as P8; its construction recipe is shown at P8.
PROVENANCE & LICENSES
A FreeCAD (.FCStd) document from a public repository crawl; recipes are the document's own serialized feature recipes (and, for linked parts, companion documents' recipes).
License: mit.
